# Revit family: Building-IEC309Connections-GEWISS-IEC309HP-90°_SURFACE_MOUNT_INLET_32A_IP44
name_source: partatom
category: Apparecchi elettrici
units: mm (PartAtom-declared; Revit-internal decimal feet)

## family parameters
Condiviso = Sì
Host = Superficie
Mantenere orientamento annotazione = Sì
Punto di calcolo locali = Sì
Quota connettore circolare = Usa diametro
Taglio con vuoti quando caricato = No
Tipo di parte = Normale

## types (11) — shared parameters
BLOCCO = B=C
Breaking capacity at 1.1 Un = 40A
Catalogue = BUILDING
Corpo centrale = Default(2)
Electrocod = 2230
FORMULA = 1000 mm  [stored 3.28084 ft]
Frequency = 50/60 Hz
Glow wire test: = 850 °C (active parts) - 650 °C (passive parts)
IDF = 1e4aea71-56ca-41c1-95df-ac7f5278f8eb
IDT = 090f4c021f2946f5a1957219c5884a63
IP degree = IP44
Immagine tipo = <Nessuno>
Insulation resistance = - 10 M?
L = 155 mm
Operating temperature: = -25 +55 °C
Permissible overload = 42A
Piastra = Default(2)
Produttore = GEWISS S.p.A.
Prospetto di default = 1219 mm
Rated current (A) = 32
SEO = Inlet
SPinotto = Default(2)
Shock resistance = IK08
Spostamento_S = 955 mm
Technical sheet = https://www.gewiss.com
Terminal tightening capacity = 2.5-6mm² flexible cables - 2.5-10mm² rigid cables
Thermo-pressure with ball = 125 °C (active parts) - 80 °C (passive parts)
Total number of operations = -2000
Type of wiring = With screw
Typology = 90° angled surface mounting inlet
URL = https://www.gewiss.com
Version file RFA = 21.11
W = 115 mm

## per-type parameters (varying)
| type | Colour: | Descrizione | Modello | No. of poles | Rated voltage | Reference h |
| GW60413 - IP44 90°APPL.INLET 3P+E 32A 110V 4H | Yellow | IP44 90°APPL.INLET 3P+E 32A 110V 4H | GW60413 | 3P+E | 100-130V | 4 |
| GW60419 - IP44 90°APPL.INLET 3P+E 32A 400V 6H | Red | IP44 90°APPL.INLET 3P+E 32A 400V 6H | GW60419 | 3P+E | 380-415V | 6 |
| GW60418 - IP44 90°APPL.INLET 2P+E 32A 400V 9H | Red | IP44 90°APPL.INLET 2P+E 32A 400V 9H | GW60418 | 2P+E | 380-415V | 9 |
| GW60417 - IP44 90°APPL.INLET 3P+N+E 32A 230V 9H | Blue | IP44 90°APPL.INLET 3P+N+E 32A 230V 9H | GW60417 | 3P+N+E | 200-250V | 9 |
| GW60416 - IP44 90°APPL.INLET 3P+E 32A 230V 9H | Blue | IP44 90°APPL.INLET 3P+E 32A 230V 9H | GW60416 | 3P+E | 200-250V | 9 |
| GW60421 - IP44 90°APPL.INLET 3P+E 32A 500V 7H | Black | IP44 90°APPL.INLET 3P+E 32A 500V 7H | GW60421 | 3P+E | 480-500V | 7 |
| GW60415 - IP44 90°APPL.INLET 2P+E 32A 230V 6H | Blue | IP44 90°APPL.INLET 2P+E 32A 230V 6H | GW60415 | 2P+E | 200-250V | 6 |
| GW60422 - IP44 90°APPL.INLET 3P+N+E 32A 500V 7H | Black | IP44 90°APPL.INLET 3P+N+E 32A 500V 7H | GW60422 | 3P+N+E | 480-500V | 7 |
| GW60414 - IP44 90°APPL.INLET 3P+N+E 32A 110V 4H | Yellow | IP44 90°APPL.INLET 3P+N+E 32A 110V 4H | GW60414 | 3P+N+E | 100-130V | 4 |
| GW60412 - IP44 90°APPL.INLET 2P+E 32A 110V 4H | Yellow | IP44 90°APPL.INLET 2P+E 32A 110V 4H | GW60412 | 2P+E | 100-130V | 4 |
| GW60420 - IP44 90°APPL.INLET 3P+N+E 32A 400V 6H | Red | IP44 90°APPL.INLET 3P+N+E 32A 400V 6H | GW60420 | 3P+N+E | 380-415V | 6 |

note: [stored X ft] marks values corroborated as IEEE doubles in the binary element streams (Revit-internal decimal feet)

## geometry (parser evidence)
native form markers: Sweep x2
no freeform markers — native parametric forms only
